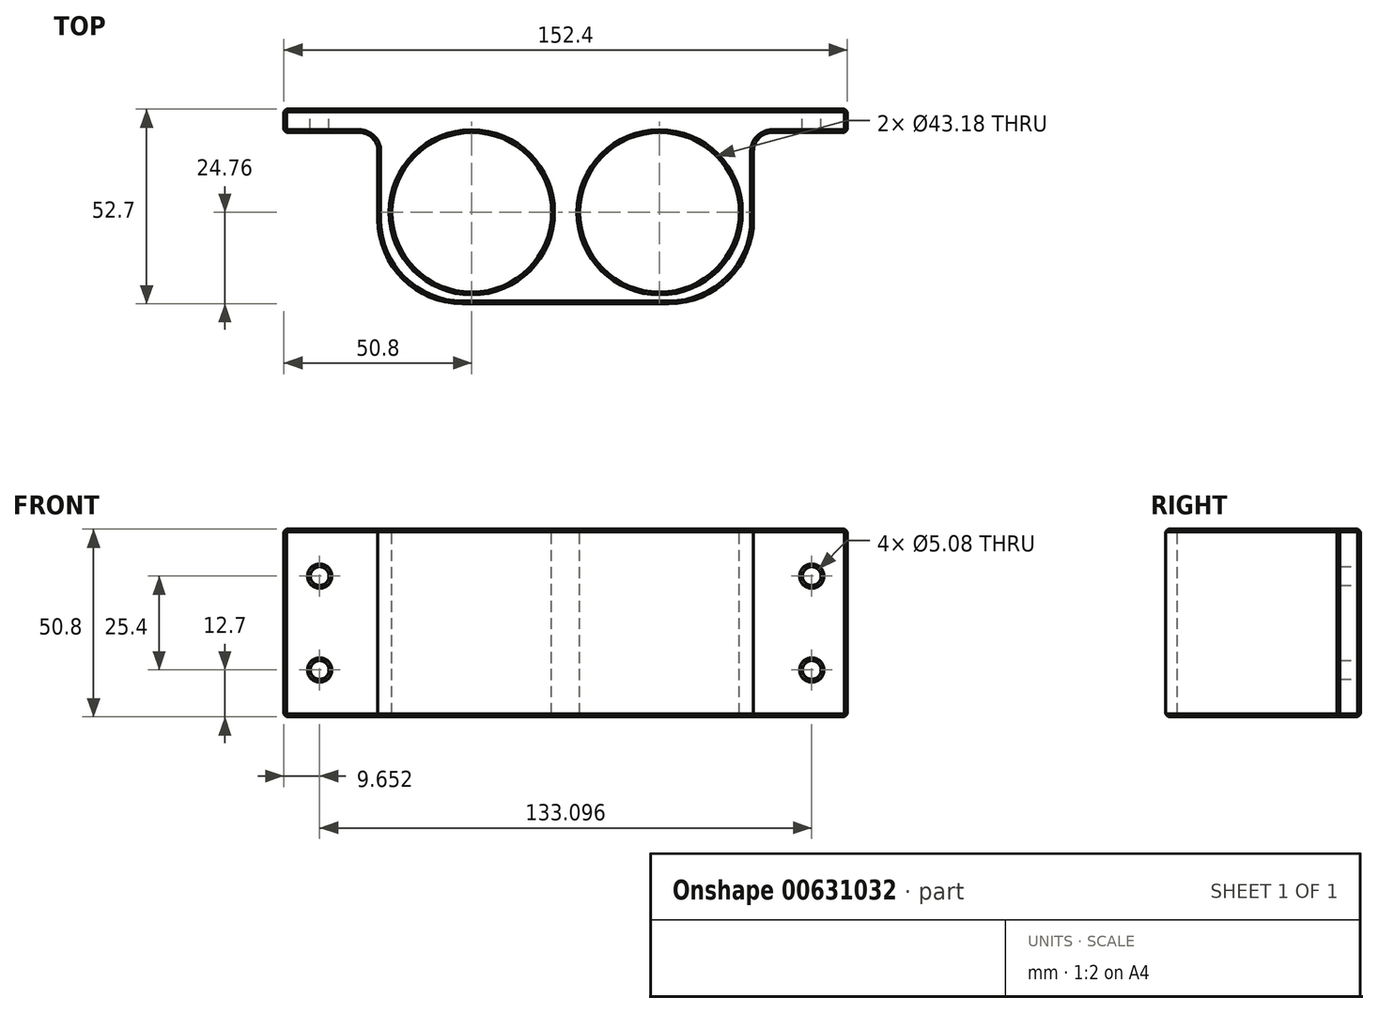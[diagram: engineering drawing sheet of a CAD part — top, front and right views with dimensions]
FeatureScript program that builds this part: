
annotation { "Feature Type Name" : "Feature", "Feature Type Description" : "" }
export const myFeature = defineFeature(function(context is Context, id is Id, definition is map)
    precondition{}
    {
        {
            var Q0;
            Q0=qCreatedBy(makeId("Front.planeOp"),FACE);
            var sketch = newSketch(context, id + "F0", { "sketchPlane" : qUnion([Q0])});
            skLineSegment(sketch, "E0.bottom", {"start": v(0, 0) * mm, "end": v(152.4, 0) * mm});
            skLineSegment(sketch, "E0.top", {"start": v(0, 50.8) * mm, "end": v(152.4, 50.8) * mm});
            skLineSegment(sketch, "E0.left", {"start": v(0, 0) * mm, "end": v(0, 50.8) * mm});
            skLineSegment(sketch, "E0.right", {"start": v(152.4, 0) * mm, "end": v(152.4, 50.8) * mm});
            skLineSegment(sketch, "E1", {"start": v(76.2, 50.8) * mm, "end": v(76.2, 0) * mm});
            skLineSegment(sketch, "E2.0", {"start": v(127, 50.8) * mm, "end": v(127, 0) * mm});
            skLineSegment(sketch, "E3.0", {"start": v(25.4, 50.8) * mm, "end": v(25.4, 0) * mm});
            skCircle(sketch, "E4", {"center": v(9.65, 38.1) * mm, "radius": 2.54 * mm});
            skCircle(sketch, "E5", {"center": v(9.65, 12.7) * mm, "radius": 2.54 * mm});
            skCircle(sketch, "E6", {"center": v(142.75, 12.7) * mm, "radius": 2.54 * mm});
            skCircle(sketch, "E7", {"center": v(142.75, 38.1) * mm, "radius": 2.54 * mm});
            skSolve(sketch);
        }
        {
            var Q0;
            {var subQ1=sQuery(id+"F0.wireOp",EDGE,"E0.left");Q0=makeQuery(id+"F0.imprint","IMPRINT",FACE,{"disambiguationData":[TD([[makeQuery(id+"F0.imprint","IMPRINT",EDGE,{"derivedFrom":subQ1}),-1.0]])]});}
            var Q1;
            {var subQ1=sQuery(id+"F0.wireOp",EDGE,"E0.right");Q1=makeQuery(id+"F0.imprint","IMPRINT",FACE,{"disambiguationData":[TD([[makeQuery(id+"F0.imprint","IMPRINT",EDGE,{"derivedFrom":subQ1}),1.0]])]});}
            var Q2;
            {var subQ0=sQuery(id+"F0.wireOp",EDGE,"E1");Q2=makeQuery(id+"F0.imprint","IMPRINT",FACE,{"disambiguationData":[TD([[makeQuery(id+"F0.imprint","IMPRINT",EDGE,{"derivedFrom":subQ0}),-1.0]])]});}
            var Q3;
            {var subQ0=sQuery(id+"F0.wireOp",EDGE,"E1");Q3=makeQuery(id+"F0.imprint","IMPRINT",FACE,{"disambiguationData":[TD([[makeQuery(id+"F0.imprint","IMPRINT",EDGE,{"derivedFrom":subQ0}),1.0]])]});}
            extrude(context, id + "F1", {"entities" : qUnion([Q0, Q1, Q2, Q3]), "depth" : 6.35 * mm, "offsetDistance" : 25.4 * mm});
        }
        {
            var Q0;
            {var subQ0=sQuery(id+"F0.wireOp",EDGE,"E1");Q0=makeQuery(id+"F0.imprint","IMPRINT",FACE,{"disambiguationData":[TD([[makeQuery(id+"F0.imprint","IMPRINT",EDGE,{"derivedFrom":subQ0}),-1.0]])]});}
            var Q1;
            {var subQ0=sQuery(id+"F0.wireOp",EDGE,"E1");Q1=makeQuery(id+"F0.imprint","IMPRINT",FACE,{"disambiguationData":[TD([[makeQuery(id+"F0.imprint","IMPRINT",EDGE,{"derivedFrom":subQ0}),1.0]])]});}
            extrude(context, id + "F2", {"entities" : qUnion([Q0, Q1]), "operationType" : NewBodyOperationType.ADD, "depth" : 52.7 * mm, "offsetDistance" : 25.4 * mm});
        }
        {
            var Q0;
            Q0=makeQuery(id+"F2.boolean.opBoolean","INTERSECT",EDGE,{"derivedFrom":[makeQuery(id+"F1.opExtrude","CAP_FACE",FACE,{"disambiguationData":[OSD([sQuery(id+"F0.wireOp",EDGE,"E0.bottom"),sQuery(id+"F0.wireOp",EDGE,"E0.top"),sQuery(id+"F0.wireOp",EDGE,"E0.left"),sQuery(id+"F0.wireOp",EDGE,"E0.right"),sQuery(id+"F0.wireOp",EDGE,"E4"),sQuery(id+"F0.wireOp",EDGE,"E5"),sQuery(id+"F0.wireOp",EDGE,"E6"),sQuery(id+"F0.wireOp",EDGE,"E7")])],"isStart":false}),makeQuery(id+"F2.opExtrude","SWEPT_FACE",FACE,{"disambiguationData":[OSD([sQuery(id+"F0.wireOp",EDGE,"E2.0")])]})]});
            var Q1;
            Q1=makeQuery(id+"F2.boolean.opBoolean","INTERSECT",EDGE,{"derivedFrom":[makeQuery(id+"F1.opExtrude","CAP_FACE",FACE,{"disambiguationData":[OSD([sQuery(id+"F0.wireOp",EDGE,"E0.bottom"),sQuery(id+"F0.wireOp",EDGE,"E0.top"),sQuery(id+"F0.wireOp",EDGE,"E0.left"),sQuery(id+"F0.wireOp",EDGE,"E0.right"),sQuery(id+"F0.wireOp",EDGE,"E4"),sQuery(id+"F0.wireOp",EDGE,"E5"),sQuery(id+"F0.wireOp",EDGE,"E6"),sQuery(id+"F0.wireOp",EDGE,"E7")])],"isStart":false}),makeQuery(id+"F2.opExtrude","SWEPT_FACE",FACE,{"disambiguationData":[OSD([sQuery(id+"F0.wireOp",EDGE,"E3.0")])]})]});
            fillet(context, id + "F3", {"entities" : qUnion([Q0, Q1]), "radius" : 5.08 * mm, "tangentPropagation" : true, "allowEdgeOverflow" : false});
        }
        {
            var Q0;
            {var subQ0=sQuery(id+"F0.wireOp",EDGE,"E0.top");Q0=makeQuery(id+"F2.boolean.opBoolean","MERGE",FACE,{"derivedFrom":[makeQuery(id+"F1.opExtrude","SWEPT_FACE",FACE,{"disambiguationData":[OSD([subQ0])]}),makeQuery(id+"F2.opExtrude","SWEPT_FACE",FACE,{"disambiguationData":[OSD([subQ0])]})]});}
            var sketch = newSketch(context, id + "F4", { "sketchPlane" : qUnion([Q0])});
            skPoint(sketch, "E8.centerSnap0", {"position": v(76.2, 0) * mm});
            skCircle(sketch, "E9", {"center": v(50.8, -27.94) * mm, "radius": 21.59 * mm});
            skCircle(sketch, "E10", {"center": v(101.6, -27.94) * mm, "radius": 21.59 * mm});
            skSolve(sketch);
        }
        {
            var Q0;
            Q0=makeQuery(id+"F4.imprint","IMPRINT",FACE,{"disambiguationData":[TD([[makeQuery(id+"F4.imprint","IMPRINT",EDGE,{"derivedFrom":sQuery(id+"F4.wireOp",EDGE,"E9")}),1.0]])]});
            var Q1;
            Q1=makeQuery(id+"F4.imprint","IMPRINT",FACE,{"disambiguationData":[TD([[makeQuery(id+"F4.imprint","IMPRINT",EDGE,{"derivedFrom":sQuery(id+"F4.wireOp",EDGE,"E10")}),1.0]])]});
            extrude(context, id + "F5", {"entities" : qUnion([Q0, Q1]), "operationType" : NewBodyOperationType.REMOVE, "endBound" : BoundingType.THROUGH_ALL, "oppositeDirection" : true, "depth" : 44.45 * mm, "offsetDistance" : 25.4 * mm});
        }
        {
            var Q0;
            Q0=makeQuery(id+"F2.opExtrude","CAP_EDGE",EDGE,{"disambiguationData":[OSD([sQuery(id+"F0.wireOp",EDGE,"E2.0")])],"isStart":false});
            var Q1;
            Q1=makeQuery(id+"F2.opExtrude","CAP_EDGE",EDGE,{"disambiguationData":[OSD([sQuery(id+"F0.wireOp",EDGE,"E3.0")])],"isStart":false});
            fillet(context, id + "F6", {"entities" : qUnion([Q0, Q1]), "radius" : 22.86 * mm, "tangentPropagation" : true, "allowEdgeOverflow" : false});
        }
        {
            var Q0;
            {var subQ0=sQuery(id+"F0.wireOp",EDGE,"E0.top");Q0=makeQuery(id+"F2.boolean.opBoolean","MERGE",FACE,{"derivedFrom":[makeQuery(id+"F1.opExtrude","SWEPT_FACE",FACE,{"disambiguationData":[OSD([subQ0])]}),makeQuery(id+"F2.opExtrude","SWEPT_FACE",FACE,{"disambiguationData":[OSD([subQ0])]})]});}
            var Q1;
            {var subQ0=sQuery(id+"F0.wireOp",EDGE,"E4");var subQ1=sQuery(id+"F0.wireOp",EDGE,"E0.left");var subQ2=sQuery(id+"F0.wireOp",EDGE,"E0.bottom");var subQ3=sQuery(id+"F0.wireOp",EDGE,"E0.top");var subQ4=sQuery(id+"F0.wireOp",EDGE,"E5");Q1=makeQuery(id+"F2.boolean.opBoolean","SPLIT",FACE,{"disambiguationData":[TD([makeQuery(id+"F1.opExtrude","SWEPT_FACE",FACE,{"disambiguationData":[OSD([subQ1])]})])],"derivedFrom":makeQuery(id+"F1.opExtrude","CAP_FACE",FACE,{"disambiguationData":[OSD([subQ2,subQ3,subQ1,sQuery(id+"F0.wireOp",EDGE,"E0.right"),subQ0,subQ4,sQuery(id+"F0.wireOp",EDGE,"E6"),sQuery(id+"F0.wireOp",EDGE,"E7")])],"isStart":false})});}
            var Q2;
            {var subQ0=sQuery(id+"F0.wireOp",EDGE,"E6");var subQ1=sQuery(id+"F0.wireOp",EDGE,"E0.top");var subQ2=sQuery(id+"F0.wireOp",EDGE,"E0.right");var subQ3=sQuery(id+"F0.wireOp",EDGE,"E0.bottom");var subQ4=sQuery(id+"F0.wireOp",EDGE,"E7");Q2=makeQuery(id+"F2.boolean.opBoolean","SPLIT",FACE,{"disambiguationData":[TD([makeQuery(id+"F1.opExtrude","SWEPT_FACE",FACE,{"disambiguationData":[OSD([subQ2])]})])],"derivedFrom":makeQuery(id+"F1.opExtrude","CAP_FACE",FACE,{"disambiguationData":[OSD([subQ3,subQ1,sQuery(id+"F0.wireOp",EDGE,"E0.left"),subQ2,sQuery(id+"F0.wireOp",EDGE,"E4"),sQuery(id+"F0.wireOp",EDGE,"E5"),subQ0,subQ4])],"isStart":false})});}
            var Q3;
            {var subQ0=sQuery(id+"F0.wireOp",EDGE,"E0.bottom");Q3=makeQuery(id+"F2.boolean.opBoolean","MERGE",FACE,{"derivedFrom":[makeQuery(id+"F1.opExtrude","SWEPT_FACE",FACE,{"disambiguationData":[OSD([subQ0])]}),makeQuery(id+"F2.opExtrude","SWEPT_FACE",FACE,{"disambiguationData":[OSD([subQ0])]})]});}
            var Q4;
            Q4=makeQuery(id+"F1.opExtrude","CAP_FACE",FACE,{"disambiguationData":[OSD([sQuery(id+"F0.wireOp",EDGE,"E0.bottom"),sQuery(id+"F0.wireOp",EDGE,"E0.top"),sQuery(id+"F0.wireOp",EDGE,"E0.left"),sQuery(id+"F0.wireOp",EDGE,"E0.right"),sQuery(id+"F0.wireOp",EDGE,"E4"),sQuery(id+"F0.wireOp",EDGE,"E5"),sQuery(id+"F0.wireOp",EDGE,"E6"),sQuery(id+"F0.wireOp",EDGE,"E7")])],"isStart":true});
            var Q5;
            Q5=makeQuery(id+"F5.boolean.opBoolean","COPY",EDGE,{"derivedFrom":makeQuery(id+"F5.opExtrude","CAP_EDGE",EDGE,{"disambiguationData":[OSD([sQuery(id+"F4.wireOp",EDGE,"E9")])],"isStart":false})});
            var Q6;
            Q6=makeQuery(id+"F5.boolean.opBoolean","COPY",EDGE,{"derivedFrom":makeQuery(id+"F5.opExtrude","CAP_EDGE",EDGE,{"disambiguationData":[OSD([sQuery(id+"F4.wireOp",EDGE,"E10")])],"isStart":false})});
            chamfer(context, id + "F7", {"entities" : qUnion([Q0, Q1, Q2, Q3, Q4, Q5, Q6]), "width" : 0.76 * mm, "tangentPropagation" : true});
        }
    });
